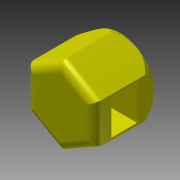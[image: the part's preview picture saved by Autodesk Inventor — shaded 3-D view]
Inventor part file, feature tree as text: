
AUTODESK INVENTOR PART (.ipt)
format: ipt  version: 2013 (Build 170138000, 138)  size: 155,648 bytes
history: native  units: in
note: dims shown in document units (in); Inventor stores cm internally (conversion verified against a paired STEP export)
features: extrude x5, sketch x5, fillet x1
ambient origin geometry x8: Origin, YZ Plane, XZ Plane, XY Plane, X Axis, Y Axis, Z Axis, Center Point
bodies: Solid1 (feature_tree)
feature tree (11):
  extrude  "Extrusion1"  Depth=0.25in TaperAngle=0.0deg
  extrude  "Extrusion2"  Depth=0.375in TaperAngle=0.0deg
  extrude  "Extrusion3"  Depth=0.25in TaperAngle=30.0deg
  extrude  "Extrusion4"  Depth=0.25in TaperAngle=0.0deg
  extrude  "Extrusion5"  [1 undecoded]
  fillet  "Fillet1"  [1 undecoded]
  sketch  "Sketch1"  dims[d0=1.0in d1=0.25in d2=0.0in]
  sketch  "Sketch2"  dims[d3=0.515in d4=0.375in d5=0.0in]
  sketch  "Sketch3"  dims[d6=0.25in d7=0.0in d10=0.25in d11=30.0deg]
  sketch  "Sketch4"  dims[d13=0.3438in d15=0.25in d16=0.0in]
  sketch  "Sketch5"  dims[d17=0.125in]
note: 2 required parameter values undecoded (feature->parameter linkage not recoverable at this tier; creation-order binding heuristic only, values carry confidence <= 0.55)
